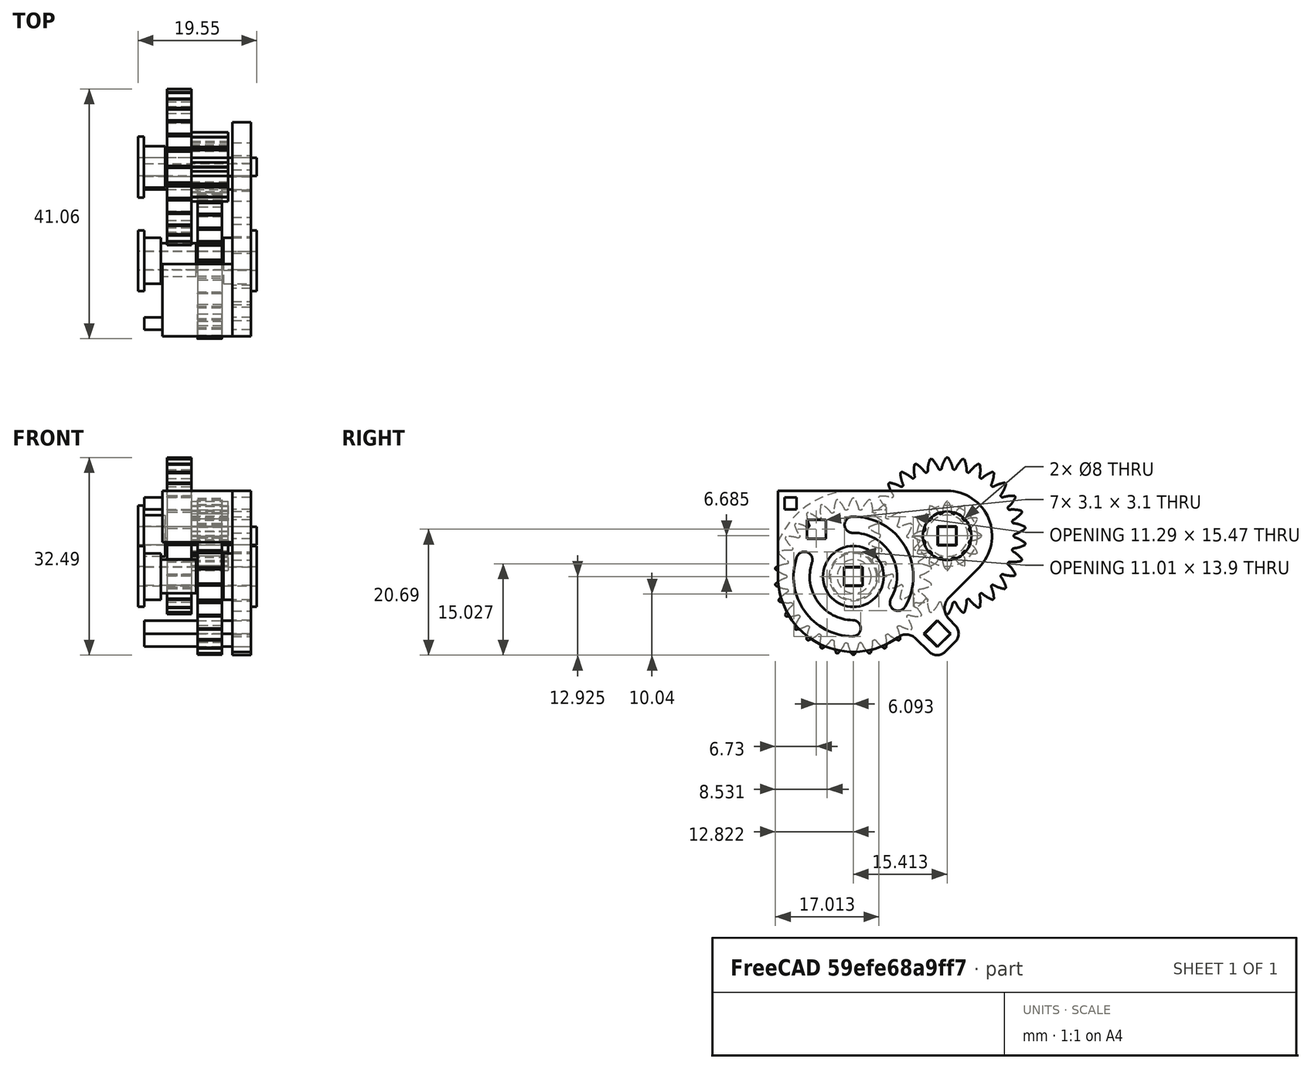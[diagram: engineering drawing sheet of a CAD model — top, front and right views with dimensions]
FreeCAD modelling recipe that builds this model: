
FCSTD DOCUMENT  (FreeCAD 1.1R14555 (Git shallow))
Label: testbuild
License: All rights reserved
LicenseURL: https://en.wikipedia.org/wiki/All_rights_reserved
objects: Sketcher::SketchObject×17, App::Point×14, PartDesign::Body×13, PartDesign::Pad×13, PartDesign::SubShapeBinder×6, App::Link×3, PartDesign::FeaturePython×3, PartDesign::Pocket×3, PartDesign::Point×3, App::FeaturePython×2, Assembly::JointGroup×1, Assembly::AssemblyObject×1, Part::DatumPoint×1, PartDesign::FeatureBase×1, App::DocumentObjectGroup×1
note: 112 computed .brp shape members not serialized (recipe doc carries the construction recipe); baked Part::Feature solids carry a one-line shape summary decoded from their .brp
EXTERNAL_REF file=../toy_motor_with_body.FCStd obj=Body
EXTERNAL_REF file=../dot8_worm_gear .FCStd obj=Body007
EXTERNAL_REF file=../toy_motor_with_body.FCStd obj=Body001

FEATURE [App::Link] toymotor
  LinkedObject = -> <external ../toy_motor_with_body.FCStd>#Body
FEATURE [App::FeaturePython] GroundedJoint  # Assembly grounded joint (typed FeaturePython)
  ObjectToGround = -> toymotor
FEATURE [App::Link] dot8_worm_gear
  LinkPlacement = pos=(-5.5e-15,18.25,2.4e-15) rot=(-0.41468,0.643445,0.643444;2.3554rad)
  LinkedObject = -> <external ../dot8_worm_gear .FCStd>#Body007
  Placement = pos=(-5.5e-15,18.25,2.4e-15) rot=(-0.41468,0.643445,0.643444;2.3554rad)
FEATURE [PartDesign::FeaturePython] InvoluteGear  # WARN: FeaturePython — macro-defined, semantics opaque (R4)
  AttacherType = Attacher::AttachEngine3D
  Suppressed = false
  addendum_diameter = 25.76
  angular_backlash = 0
  axle_hole = true
  axle_holesize = 2.09
  backlash = 0
  clearance = 0.3
  double_helix = false
  head = 0.1
  head_fillet = 0
  height = 4
  helix_angle = 0
  module = 0.8
  num_teeth = 30
  numpoints = 20
  offset_hole = false
  offset_holeoffset = 10
  offset_holesize = 10
  pitch_diameter = 24
  pressure_angle = 26
  properties_from_tool = false
  reversed_backlash = false
  root_diameter = 21.92
  root_fillet = 0.3
  shift = 0
  simple = false
  transverse_pitch = 2.51327
  traverse_module = 0.8
  undercut = false
  version = 1.3.0
  expr: angular_backlash = backlash / pitch_diameter * 360 ° / pi
FEATURE [PartDesign::FeaturePython] InvoluteGear001  # WARN: FeaturePython — macro-defined, semantics opaque (R4)
  AttacherType = Attacher::AttachEngine3D
  Suppressed = false
  addendum_diameter = 11.36
  angular_backlash = 0
  axle_hole = true
  axle_holesize = 2.09
  backlash = 0
  clearance = 0.3
  double_helix = false
  head = 0.1
  head_fillet = 0
  height = 6
  helix_angle = 0
  module = 0.8
  num_teeth = 12
  numpoints = 20
  offset_hole = false
  offset_holeoffset = 10
  offset_holesize = 10
  pitch_diameter = 9.6
  pressure_angle = 27
  properties_from_tool = false
  reversed_backlash = false
  root_diameter = 7.52
  root_fillet = 0.4
  shift = 0
  simple = false
  transverse_pitch = 2.51327
  traverse_module = 0.8
  undercut = false
  version = 1.3.0
  expr: angular_backlash = backlash / pitch_diameter * 360 ° / pi
FEATURE [PartDesign::FeaturePython] InvoluteGear002  # WARN: FeaturePython — macro-defined, semantics opaque (R4)
  AttacherType = Attacher::AttachEngine3D
  Suppressed = false
  addendum_diameter = 25.76
  angular_backlash = 0
  axle_hole = true
  axle_holesize = 2.09
  backlash = 0
  clearance = 0.3
  double_helix = false
  head = 0.1
  head_fillet = 0
  height = 4
  helix_angle = 0
  module = 0.8
  num_teeth = 30
  numpoints = 20
  offset_hole = false
  offset_holeoffset = 10
  offset_holesize = 10
  pitch_diameter = 24
  pressure_angle = 26
  properties_from_tool = false
  reversed_backlash = false
  root_diameter = 21.92
  root_fillet = 0.3
  shift = 0
  simple = false
  transverse_pitch = 2.51327
  traverse_module = 0.8
  undercut = false
  version = 1.3.0
  expr: angular_backlash = backlash / pitch_diameter * 360 ° / pi
FEATURE [App::FeaturePython] Joint009  label="Revolute002"  # Assembly joint (typed FeaturePython)
  Angle = 0
  AngleMax = 0
  AngleMin = 0
  Detach1 = false
  Detach2 = false
  Distance = 0
  Distance2 = 0
  EnableAngleMax = false
  EnableAngleMin = false
  EnableLengthMax = false
  EnableLengthMin = false
  JointType = 1 (Revolute)
  LengthMax = 0
  LengthMin = 0
  Offset2 = pos=(0,0,-7) rot=(0,0,1;0rad)
  Placement1 = pos=(0,21.25,0) rot=(-1,0,0;1.5708rad)
  Placement2 = pos=(-8.07778e-06,1.0786e-06,2.99997) rot=(-0.13236,-0.991265,0;3e-06rad)
  Reference1 = -> Assembly [toymotor.Edge79,toymotor.Edge79]
  Reference2 = -> Assembly [dot8_worm_gear.Edge14,dot8_worm_gear.Edge14]
  Suppressed = false
FEATURE [Assembly::JointGroup] Joints
  Group = -> [GroundedJoint,Joint009]
FEATURE [App::Link] toymotor_body  label="toymotor.body"
  LinkPlacement = pos=(4e-15,4.2e-15,-3.5e-15) rot=(0,0,1;0rad)
  LinkedObject = -> <external ../toy_motor_with_body.FCStd>#Body001
  Placement = pos=(4e-15,4.2e-15,-3.5e-15) rot=(0,0,1;0rad)
FEATURE [Assembly::AssemblyObject] Assembly
  Group = -> [Joints,toymotor,GroundedJoint,toymotor_body,dot8_worm_gear,Joint009]
  Origin = -> Origin001
  Type = Assembly
FEATURE [Sketcher::SketchObject] Sketch006
  ArcFitTolerance = 1e-06
  AttachmentSupport = -> [InvoluteGear001]
  ExternalTypes = [0]
  FullyConstrained = true
  MakeInternals = false
  MapMode = 5
  Placement = pos=(0,0,6) rot=(0,0,1;0rad)
  sketch-geometry (5):
    g0: LineSegment StartX=-1.55 StartY=-1.55 StartZ=0 EndX=1.55 EndY=-1.55 EndZ=0
    g1: LineSegment StartX=1.55 StartY=-1.55 StartZ=0 EndX=1.55 EndY=1.55 EndZ=0
    g2: LineSegment StartX=1.55 StartY=1.55 StartZ=0 EndX=-1.55 EndY=1.55 EndZ=0
    g3: LineSegment StartX=-1.55 StartY=1.55 StartZ=0 EndX=-1.55 EndY=-1.55 EndZ=0
    g4: GeomPoint [constr] X=0 Y=0 Z=0
  constraints (12):
    c: Coincident(g0,g1)
    c: Coincident(g1,g2)
    c: Coincident(g2,g3)
    c: Coincident(g3,g0)
    c: Horizontal(g0)
    c: Horizontal(g2)
    c: Vertical(g1)
    c: Vertical(g3)
    c: Symmetric(g2,g0,g4)
    c: Coincident(g4,g-1)
    c: Equal(g2,g1)
    c: Distance(g2,g2) = 3.1
FEATURE [PartDesign::Pocket] Pocket001
  BaseFeature = -> InvoluteGear001
  Direction = (0,0,-1)
  Length = 5
  Length2 = 5
  Profile = -> Sketch006
  ReferenceAxis = -> Sketch006 [N_Axis]
  Refine = true
  SideType = 0
  Suppressed = false
  Type = 1
  Type2 = 0
FEATURE [Sketcher::SketchObject] Sketch007
  ArcFitTolerance = 1e-06
  AttachmentSupport = -> [InvoluteGear]
  ExternalTypes = [0]
  FullyConstrained = true
  MakeInternals = false
  MapMode = 5
  Placement = pos=(0,0,4) rot=(0,0,1;0rad)
  sketch-geometry (5):
    g0: LineSegment StartX=-1.55 StartY=1.55 StartZ=0 EndX=-1.55 EndY=-1.55 EndZ=0
    g1: LineSegment StartX=-1.55 StartY=-1.55 StartZ=0 EndX=1.55 EndY=-1.55 EndZ=0
    g2: LineSegment StartX=1.55 StartY=-1.55 StartZ=0 EndX=1.55 EndY=1.55 EndZ=0
    g3: LineSegment StartX=1.55 StartY=1.55 StartZ=0 EndX=-1.55 EndY=1.55 EndZ=0
    g4: GeomPoint [constr] X=0 Y=0 Z=0
  constraints (12):
    c: Coincident(g0,g1)
    c: Coincident(g1,g2)
    c: Coincident(g2,g3)
    c: Coincident(g3,g0)
    c: Vertical(g0)
    c: Vertical(g2)
    c: Horizontal(g1)
    c: Horizontal(g3)
    c: Symmetric(g2,g0,g4)
    c: Coincident(g4,g-1)
    c: Equal(g3,g2)
    c: Distance(g3,g3) = 3.1
FEATURE [PartDesign::Pocket] Pocket
  BaseFeature = -> InvoluteGear
  Direction = (0,0,-1)
  Length = 5
  Length2 = 5
  Profile = -> Sketch007
  ReferenceAxis = -> Sketch007 [N_Axis]
  Refine = true
  SideType = 0
  Suppressed = false
  Type = 1
  Type2 = 0
FEATURE [Sketcher::SketchObject] Sketch
  ArcFitTolerance = 1e-06
  AttachmentSupport = -> [InvoluteGear002]
  ExternalTypes = [0]
  FullyConstrained = true
  MakeInternals = false
  MapMode = 5
  Placement = pos=(0,0,4) rot=(0,0,1;0rad)
  sketch-geometry (5):
    g0: LineSegment StartX=1.55 StartY=1.55 StartZ=0 EndX=-1.55 EndY=1.55 EndZ=0
    g1: LineSegment StartX=-1.55 StartY=1.55 StartZ=0 EndX=-1.55 EndY=-1.55 EndZ=0
    g2: LineSegment StartX=-1.55 StartY=-1.55 StartZ=0 EndX=1.55 EndY=-1.55 EndZ=0
    g3: LineSegment StartX=1.55 StartY=-1.55 StartZ=0 EndX=1.55 EndY=1.55 EndZ=0
    g4: GeomPoint [constr] X=0 Y=0 Z=0
  constraints (12):
    c: Coincident(g0,g1)
    c: Coincident(g1,g2)
    c: Coincident(g2,g3)
    c: Coincident(g3,g0)
    c: Horizontal(g0)
    c: Horizontal(g2)
    c: Vertical(g1)
    c: Vertical(g3)
    c: Symmetric(g2,g0,g4)
    c: Coincident(g4,g-1)
    c: Equal(g3,g0)
    c: Distance(g0,g0) = 3.1
FEATURE [PartDesign::Pocket] Pocket002
  BaseFeature = -> InvoluteGear002
  Direction = (0,0,-1)
  Length = 5
  Length2 = 5
  Profile = -> Sketch
  ReferenceAxis = -> Sketch [N_Axis]
  Refine = true
  SideType = 0
  Suppressed = false
  Type = 1
  Type2 = 0
FEATURE [Sketcher::SketchObject] Sketch008
  ArcFitTolerance = 1e-06
  ExternalTypes = [0]
  FullyConstrained = false
  MakeInternals = false
  Placement = pos=(0,0,0) rot=(0.57735,0.57735,0.57735;2.0944rad)
  sketch-geometry (5):
    g0: LineSegment StartX=0 StartY=0 StartZ=0 EndX=25.3053 EndY=0 EndZ=0
    g1: LineSegment StartX=25.3053 StartY=-16.23 StartZ=0 EndX=9.89253 EndY=-22.9148 EndZ=0
    g2: LineSegment StartX=9.89253 StartY=-22.9148 StartZ=0 EndX=0 EndY=0 EndZ=0
    g3: LineSegment StartX=25.3053 StartY=0 StartZ=0 EndX=25.3053 EndY=-4.23 EndZ=0
    g4: LineSegment StartX=25.3053 StartY=-4.23 StartZ=0 EndX=25.3053 EndY=-16.23 EndZ=0
  constraints (12):
    c: Coincident(g0,g-1)
    c: PointOnObject(g0,g-1)
    c: Coincident(g1,g4)
    c: Coincident(g2,g1)
    c: Coincident(g2,g0)
    c: Distance(g1,g1) = 16.8
    c: Coincident(g3,g4)
    c: Parallel(g4,g3)
    c: Coincident(g3,g0)
    c: Vertical(g3)
    c: DistanceY(g4,g4) = 12
    c: DistanceY(g3,g3) = 4.23
FEATURE [PartDesign::Body] Body004  label="master"
  AllowCompound = false
  Group = -> [Sketch008]
  Origin = -> Origin005
FEATURE [PartDesign::Point] DatumPoint003
  AttacherType = Attacher::AttachEnginePoint
  AttachmentSupport = -> [Pocket]
  MapMode = 37
  Placement = pos=(0,-1e-16,2) rot=(0,0,1;0rad)
FEATURE [PartDesign::Body] Body  label="30_inv_gear"
  AllowCompound = false
  Group = -> [InvoluteGear,Sketch007,Pocket,DatumPoint003]
  Origin = -> Origin
  Placement = pos=(2,25.3053,-16.23) rot=(0,1,0;4.71239rad)
  Tip = -> Pocket
FEATURE [PartDesign::Point] DatumPoint
  AttacherType = Attacher::AttachEnginePoint
  AttachmentSupport = -> [Pocket001]
  MapMode = 37
  Placement = pos=(2e-16,0,3) rot=(0,0,1;0rad)
FEATURE [PartDesign::Body] Body002  label="12_inv_gear"
  AllowCompound = false
  Group = -> [InvoluteGear001,Sketch006,Pocket001,DatumPoint]
  Origin = -> Origin003
  Placement = pos=(2,25.3053,-16.23) rot=(0,1,0;1.5708rad)
  Tip = -> Pocket001
FEATURE [PartDesign::Point] DatumPoint004
  AttacherType = Attacher::AttachEnginePoint
  AttachmentSupport = -> [Pocket002]
  MapMode = 37
  Placement = pos=(-2e-16,-2e-16,2) rot=(0,0,1;0rad)
FEATURE [PartDesign::Body] Body003  label="30_inv_gear001"
  AllowCompound = false
  Group = -> [InvoluteGear002,Sketch,Pocket002,DatumPoint004]
  Origin = -> Origin004
  Placement = pos=(3,9.89253,-22.9148) rot=(0,1,0;1.5708rad)
  Tip = -> Pocket002
FEATURE [App::Point] Origin006  label="Origin"
  Role = Origin
FEATURE [App::Point] Origin007  label="Origin"
  Role = Origin
FEATURE [App::Point] Origin008  label="Origin"
  Role = Origin
FEATURE [App::Point] Origin009  label="Origin"
  Role = Origin
FEATURE [App::Point] Origin010  label="Origin"
  Role = Origin
FEATURE [App::Point] Origin012
  Role = Origin
FEATURE [PartDesign::SubShapeBinder] Binder
  BindCopyOnChange = 0
  BindMode = 0
  ClaimChildren = false
  Context = -> Body005 [Binder.]
  Fuse = false
  MakeFace = true
  OffsetFill = false
  OffsetIntersection = false
  OffsetJoinType = 0
  OffsetOpenResult = false
  PartialLoad = false
  Refine = true
  Relative = true
  Support = -> [Body004[Sketch008.Edge4]]
  _Version = 2
FEATURE [Sketcher::SketchObject] Sketch009
  ArcFitTolerance = 1e-06
  AttachmentSupport = -> [Origin011]
  ExternalGeometry = -> [Binder]
  ExternalTypes = [0]
  FullyConstrained = true
  MakeInternals = false
  MapMode = 5
  Placement = pos=(0,0,0) rot=(0.57735,0.57735,0.57735;2.0944rad)
  sketch-geometry (5):
    g0: LineSegment StartX=23.8053 StartY=-14.73 StartZ=0 EndX=23.8053 EndY=-17.73 EndZ=0
    g1: LineSegment StartX=23.8053 StartY=-17.73 StartZ=0 EndX=26.8053 EndY=-17.73 EndZ=0
    g2: LineSegment StartX=26.8053 StartY=-17.73 StartZ=0 EndX=26.8053 EndY=-14.73 EndZ=0
    g3: LineSegment StartX=26.8053 StartY=-14.73 StartZ=0 EndX=23.8053 EndY=-14.73 EndZ=0
    g4: GeomPoint [constr] X=25.3053 Y=-16.23 Z=0
  constraints (12):
    c: Coincident(g0,g1)
    c: Coincident(g1,g2)
    c: Coincident(g2,g3)
    c: Coincident(g3,g0)
    c: Vertical(g0)
    c: Vertical(g2)
    c: Horizontal(g1)
    c: Horizontal(g3)
    c: Symmetric(g2,g0,g4)
    c: Coincident(g4,g-3)
    c: Equal(g2,g3)
    c: Distance(g2,g2) = 3
FEATURE [PartDesign::Pad] Pad
  Direction = (1,0,0)
  Length = 12.75
  Length2 = 6.75
  Profile = -> Sketch009
  ReferenceAxis = -> Sketch009 [N_Axis]
  Refine = true
  SideType = 1
  Suppressed = false
  Type = 0
  Type2 = 0
FEATURE [PartDesign::Body] Body005  label="30r.shaft"
  AllowCompound = false
  Group = -> [Binder,Sketch009,Pad]
  Origin = -> Origin011
  Tip = -> Pad
FEATURE [App::Point] Origin014
  Role = Origin
FEATURE [Sketcher::SketchObject] Sketch010
  ArcFitTolerance = 1e-06
  AttachmentSupport = -> [Origin013]
  ExternalTypes = [0]
  FullyConstrained = false
  MakeInternals = false
  MapMode = 5
  Placement = pos=(0,0,0) rot=(0.57735,0.57735,0.57735;2.0944rad)
  sketch-geometry (3):
    g0: ArcOfCircle CenterX=12.5467 CenterY=-13.5228 CenterZ=0 NormalX=0 NormalY=0 NormalZ=1 AngleXU=0 Radius=13.54 StartAngle=1.62123 EndAngle=2.75617
    g1: LineSegment StartX=11.8641 StartY=0 StartZ=0 EndX=0 EndY=0 EndZ=0
    g2: LineSegment StartX=0 StartY=0 StartZ=0 EndX=0 EndY=-8.43248 EndZ=0
  constraints (6):
    c: Coincident(g1,g0)
    c: Horizontal(g1)
    c: Coincident(g2,g1)
    c: Coincident(g2,g0)
    c: Vertical(g2)
    c: Coincident(g1,g-1)
FEATURE [PartDesign::Pad] Pad001
  Direction = (1,0,0)
  Length = 9.5
  Length2 = 2
  Profile = -> Sketch010
  ReferenceAxis = -> Sketch010 [N_Axis]
  Refine = true
  Reversed = true
  SideType = 1
  Suppressed = false
  Type = 0
  Type2 = 0
FEATURE [Sketcher::SketchObject] Sketch011
  ArcFitTolerance = 1e-06
  AttachmentSupport = -> [Pad001]
  ExternalGeometry = -> [Pad001]
  ExternalTypes = [0]
  FullyConstrained = true
  MakeInternals = false
  MapMode = 5
  Placement = pos=(-9.5,0,0) rot=(0.57735,-0.57735,-0.57735;2.0944rad)
  sketch-geometry (5):
    g0: LineSegment StartX=-3.06066 StartY=-1.06066 StartZ=0 EndX=-3.06066 EndY=-3.06066 EndZ=0
    g1: LineSegment StartX=-3.06066 StartY=-3.06066 StartZ=0 EndX=-1.06066 EndY=-3.06066 EndZ=0
    g2: LineSegment StartX=-1.06066 StartY=-3.06066 StartZ=0 EndX=-1.06066 EndY=-1.06066 EndZ=0
    g3: LineSegment StartX=-1.06066 StartY=-1.06066 StartZ=0 EndX=-3.06066 EndY=-1.06066 EndZ=0
    g4: LineSegment [constr] StartX=0 StartY=0 StartZ=0 EndX=-3.47298 EndY=-3.47298 EndZ=0
  constraints (15):
    c: Coincident(g0,g1)
    c: Coincident(g1,g2)
    c: Coincident(g2,g3)
    c: Coincident(g3,g0)
    c: Vertical(g0)
    c: Vertical(g2)
    c: Horizontal(g1)
    c: Horizontal(g3)
    c: Equal(g1,g2)
    c: Distance(g1,g1) = 2
    c: Coincident(g4,g-1)
    c: PointOnObject(g4,g-3)
    c: PointOnObject(g2,g4)
    c: Angle(g-1,g4) = 0.785398
    c: Distance(g2,g4) = 1.5
FEATURE [PartDesign::Pad] Pad002
  BaseFeature = -> Pad001
  Direction = (-1,0,0)
  Length = 3
  Length2 = 14.5
  Profile = -> Sketch011
  ReferenceAxis = -> Sketch011 [N_Axis]
  Refine = true
  SideType = 1
  Suppressed = false
  Type = 0
  Type2 = 0
FEATURE [PartDesign::Body] Body006  label="mobo.bom.attch"
  AllowCompound = false
  Group = -> [Sketch010,Pad001,Sketch011,Pad002]
  Origin = -> Origin013
  Placement = pos=(6.75,-2.5,-8.85) rot=(0,0,1;0rad)
  Tip = -> Pad002
FEATURE [App::Point] Origin016
  Role = Origin
FEATURE [PartDesign::SubShapeBinder] Binder001
  BindCopyOnChange = 0
  BindMode = 0
  ClaimChildren = false
  Context = -> Body007 [Binder001.]
  Fuse = false
  MakeFace = true
  OffsetFill = false
  OffsetIntersection = false
  OffsetJoinType = 0
  OffsetOpenResult = false
  PartialLoad = false
  Refine = true
  Relative = true
  Support = -> [Body006[Pad002.Face4]]
  _Version = 2
FEATURE [PartDesign::SubShapeBinder] Binder002
  BindCopyOnChange = 0
  BindMode = 0
  ClaimChildren = false
  Context = -> Body007 [Binder002.]
  Fuse = false
  MakeFace = true
  OffsetFill = false
  OffsetIntersection = false
  OffsetJoinType = 0
  OffsetOpenResult = false
  PartialLoad = false
  Refine = true
  Relative = true
  Support = -> [Body004[Sketch008.Edge4]]
  _Version = 2
FEATURE [Sketcher::SketchObject] Sketch012
  ArcFitTolerance = 1e-06
  AttachmentSupport = -> [Origin015]
  ExternalGeometry = -> [Binder001,Binder002]
  ExternalTypes = [0,0,0,0,0,0,0]
  FullyConstrained = false
  MakeInternals = false
  MapMode = 5
  Placement = pos=(0,0,0) rot=(0.57735,0.57735,0.57735;2.0944rad)
  sketch-geometry (57):
    g0: LineSegment [constr] StartX=-26.2446 StartY=-5.81934 StartZ=0 EndX=-23.2446 EndY=-5.81934 EndZ=0
    g1: LineSegment [constr] StartX=-23.2446 StartY=-5.81934 StartZ=0 EndX=-23.2446 EndY=-2.81934 EndZ=0
    g2: LineSegment [constr] StartX=-23.2446 StartY=-2.81934 StartZ=0 EndX=-26.2446 EndY=-2.81934 EndZ=0
    g3: LineSegment [constr] StartX=-26.2446 StartY=-2.81934 StartZ=0 EndX=-26.2446 EndY=-5.81934 EndZ=0
    g4: GeomPoint [constr] X=-24.7446 Y=-4.31934 Z=0
    g5: LineSegment [constr] StartX=-10.8319 StartY=-12.5042 StartZ=0 EndX=-7.83187 EndY=-12.5042 EndZ=0
    g6: LineSegment [constr] StartX=-7.83187 StartY=-12.5042 StartZ=0 EndX=-7.83187 EndY=-9.50418 EndZ=0
    g7: LineSegment [constr] StartX=-7.83187 StartY=-9.50418 StartZ=0 EndX=-10.8319 EndY=-9.50418 EndZ=0
    g8: LineSegment [constr] StartX=-10.8319 StartY=-9.50418 StartZ=0 EndX=-10.8319 EndY=-12.5042 EndZ=0
    g9: GeomPoint [constr] X=-9.33187 Y=-11.0042 Z=0
    g10: Circle [constr] CenterX=-24.7446 CenterY=-4.31934 CenterZ=0 NormalX=0 NormalY=0 NormalZ=1 AngleXU=0 Radius=2.12132
    g11: Circle [constr] CenterX=-9.33187 CenterY=-11.0042 CenterZ=0 NormalX=0 NormalY=0 NormalZ=1 AngleXU=0 Radius=2.12132
    g12: Circle CenterX=-24.7446 CenterY=-4.31934 CenterZ=0 NormalX=0 NormalY=0 NormalZ=1 AngleXU=0 Radius=4
    g13: Circle CenterX=-9.33187 CenterY=-11.0042 CenterZ=0 NormalX=0 NormalY=0 NormalZ=1 AngleXU=0 Radius=4
    g14: LineSegment StartX=3.06066 StartY=3.06066 StartZ=0 EndX=3.06066 EndY=-11.0039 EndZ=0
    g15: ArcOfCircle CenterX=-24.7446 CenterY=-4.31934 CenterZ=0 NormalX=0 NormalY=0 NormalZ=1 AngleXU=0 Radius=7.38 StartAngle=1.5708 EndAngle=3.92699
    g16: LineSegment StartX=-24.7446 StartY=3.06066 StartZ=0 EndX=3.06066 EndY=3.06066 EndZ=0
    g17: LineSegment [constr] StartX=-42.8401 StartY=-3.41976 StartZ=0 EndX=-42.8401 EndY=-6.51976 EndZ=0
    g18: LineSegment [constr] StartX=-42.8401 StartY=-6.51976 StartZ=0 EndX=-39.7401 EndY=-6.51976 EndZ=0
    g19: LineSegment [constr] StartX=-39.7401 StartY=-6.51976 StartZ=0 EndX=-39.7401 EndY=-3.41976 EndZ=0
    g20: LineSegment [constr] StartX=-39.7401 StartY=-3.41976 StartZ=0 EndX=-42.8401 EndY=-3.41976 EndZ=0
    g21: GeomPoint [constr] X=-41.2901 Y=-4.96976 Z=0
    g22: ArcOfCircle CenterX=-9.33187 CenterY=-11.0042 CenterZ=0 NormalX=0 NormalY=0 NormalZ=1 AngleXU=0 Radius=12.3925 StartAngle=4.07512 EndAngle=6.28321
    g23: LineSegment StartX=-20.9101 StartY=-20.3929 StartZ=0 EndX=-23.1021 EndY=-18.2009 EndZ=0
    g24: LineSegment StartX=-23.1021 StartY=-18.2009 StartZ=0 EndX=-25.2941 EndY=-20.3929 EndZ=0
    g25: LineSegment StartX=-25.2941 StartY=-20.3929 StartZ=0 EndX=-23.1021 EndY=-22.5849 EndZ=0
    g26: LineSegment StartX=-23.1021 StartY=-22.5849 StartZ=0 EndX=-20.9101 EndY=-20.3929 EndZ=0
    g27: Circle [constr] CenterX=-23.1021 CenterY=-20.3929 CenterZ=0 NormalX=0 NormalY=0 NormalZ=1 AngleXU=0 Radius=2.19203
    g28: LineSegment StartX=-29.9631 StartY=-9.53779 StartZ=0 EndX=-25.0578 EndY=-14.4431 EndZ=0
    g29: LineSegment StartX=-25.0578 StartY=-18.0359 StartZ=0 EndX=-26.0847 EndY=-19.0627 EndZ=0
    g30: LineSegment StartX=-26.0847 StartY=-21.7237 StartZ=0 EndX=-24.4326 EndY=-23.3758 EndZ=0
    g31: LineSegment StartX=-21.7716 StartY=-23.3758 StartZ=0 EndX=-19.573 EndY=-21.1771 EndZ=0
    g32: ArcOfCircle CenterX=-26.8542 CenterY=-16.2395 CenterZ=0 NormalX=0 NormalY=0 NormalZ=1 AngleXU=0 Radius=2.54048 StartAngle=5.49779 EndAngle=7.06858
    g33: GeomPoint [constr] X=-23.2614 Y=-16.2395 Z=0
    g34: ArcOfCircle CenterX=-24.7542 CenterY=-20.3932 CenterZ=0 NormalX=0 NormalY=0 NormalZ=1 AngleXU=0 Radius=1.88157 StartAngle=2.35619 EndAngle=3.92699
    g35: GeomPoint [constr] X=-27.4151 Y=-20.3932 Z=0
    g36: ArcOfCircle CenterX=-23.1021 CenterY=-22.0453 CenterZ=0 NormalX=0 NormalY=0 NormalZ=1 AngleXU=0 Radius=1.88157 StartAngle=3.92699 EndAngle=5.49779
    g37: GeomPoint [constr] X=-23.1021 Y=-24.7063 Z=0
    g38: GeomPoint [constr] X=-17.4845 Y=-19.4449 Z=0
    g39: ArcOfCircle CenterX=-18.0158 CenterY=-22.7344 CenterZ=0 NormalX=0 NormalY=0 NormalZ=1 AngleXU=0 Radius=2.20224 StartAngle=0.933529 EndAngle=2.35619
    g40: LineSegment [constr] StartX=-25 StartY=-22.8084 StartZ=0 EndX=-23.9393 EndY=-21.7477 EndZ=0
    g41: LineSegment [constr] StartX=-21.8706 StartY=-21.3535 StartZ=0 EndX=-20.81 EndY=-22.4141 EndZ=0
    g42: ArcOfCircle CenterX=-9.33187 CenterY=-11.0042 CenterZ=0 NormalX=0 NormalY=0 NormalZ=1 AngleXU=0 Radius=9.83608 StartAngle=1.55622 EndAngle=3.67351
    g43: ArcOfCircle CenterX=-16.6618 CenterY=-15.3178 CenterZ=0 NormalX=0 NormalY=0 NormalZ=1 AngleXU=0 Radius=1.33107 StartAngle=3.67351 EndAngle=6.8151
    g44: ArcOfCircle CenterX=-9.20792 CenterY=-2.50008 CenterZ=0 NormalX=0 NormalY=0 NormalZ=1 AngleXU=0 Radius=1.33107 StartAngle=4.69781 EndAngle=7.83941
    g45: ArcOfCircle CenterX=-9.33187 CenterY=-11.0042 CenterZ=0 NormalX=0 NormalY=0 NormalZ=1 AngleXU=0 Radius=7.17393 StartAngle=1.55622 EndAngle=3.67351
    g46: ArcOfCircle CenterX=-9.33187 CenterY=-11.0042 CenterZ=0 NormalX=0 NormalY=0 NormalZ=1 AngleXU=0 Radius=9.83608 StartAngle=4.72652 EndAngle=6.61075
    g47: ArcOfCircle CenterX=-9.21166 CenterY=-19.5083 CenterZ=0 NormalX=0 NormalY=0 NormalZ=1 AngleXU=0 Radius=1.33107 StartAngle=1.58493 EndAngle=4.72652
    g48: ArcOfCircle CenterX=-1.2791 CenterY=-8.26776 CenterZ=0 NormalX=0 NormalY=0 NormalZ=1 AngleXU=0 Radius=1.33107 StartAngle=0.327569 EndAngle=3.46916
    g49: ArcOfCircle CenterX=-9.33187 CenterY=-11.0042 CenterZ=0 NormalX=0 NormalY=0 NormalZ=1 AngleXU=0 Radius=7.17393 StartAngle=4.72652 EndAngle=6.61075
    g50: LineSegment StartX=-4.78934 StartY=-1.68934 StartZ=0 EndX=-4.78934 EndY=-4.78934 EndZ=0
    g51: LineSegment StartX=-4.78934 StartY=-4.78934 StartZ=0 EndX=-1.68934 EndY=-4.78934 EndZ=0
    g52: LineSegment StartX=-1.68934 StartY=-4.78934 StartZ=0 EndX=-1.68934 EndY=-1.68934 EndZ=0
    g53: LineSegment StartX=-1.68934 StartY=-1.68934 StartZ=0 EndX=-4.78934 EndY=-1.68934 EndZ=0
    g54: GeomPoint [constr] X=-3.23934 Y=-3.23934 Z=0
    g55: LineSegment [constr] StartX=-28.6445 StartY=-18.2009 StartZ=0 EndX=-18.0503 EndY=-18.2009 EndZ=0
    g56: LineSegment [constr] StartX=-25.6512 StartY=-18.6293 StartZ=0 EndX=-24.5647 EndY=-19.6635 EndZ=0
  constraints (124):
    c: Coincident(g0,g1)
    c: Coincident(g1,g2)
    c: Coincident(g2,g3)
    c: Coincident(g3,g0)
    c: Horizontal(g0)
    c: Horizontal(g2)
    c: Vertical(g1)
    c: Vertical(g3)
    c: Symmetric(g2,g0,g4)
    c: Distance(g0,g2) = 3
    c: Coincident(g4,g-7)
    c: Coincident(g5,g6)
    c: Coincident(g6,g7)
    c: Coincident(g7,g8)
    c: Coincident(g8,g5)
    c: Horizontal(g5)
    c: Horizontal(g7)
    c: Vertical(g6)
    c: Vertical(g8)
    c: Symmetric(g7,g5,g9)
    c: Coincident(g9,g-7)
    c: Equal(g1,g2)
    c: Equal(g7,g6)
    c: Equal(g1,g7)
    c: Coincident(g10,g4)
    c: Coincident(g11,g9)
    c: Equal(g10,g11)
    c: PointOnObject(g1,g10)
    c: Coincident(g12,g4)
    c: Coincident(g13,g9)
    c: Coincident(g14,g-11)
    c: Vertical(g14)
    c: Coincident(g15,g4)
    c: Coincident(g16,g14)
    c: Horizontal(g16)
    c: Tangent(g16,g15) = 1.5708
    c: Coincident(g22,g14) = 1.5708
    c: Coincident(g17,g18)
    c: Coincident(g18,g19)
    c: Coincident(g19,g20)
    c: Coincident(g20,g17)
    c: Vertical(g17)
    c: Vertical(g19)
    c: Horizontal(g18)
    c: Horizontal(g20)
    c: Symmetric(g19,g17,g21)
    c: Distance(g17,g19) = 3.1
    c: Equal(g19,g20)
    c: Coincident(g9,g22)
    c: Coincident(g23,g24)
    c: Coincident(g24,g25)
    c: Coincident(g25,g26)
    c: Coincident(g26,g23)
    c: Equal(g23,g24)
    c: Equal(g23,g25)
    c: Equal(g23,g26)
    c: PointOnObject(g23,g27)
    c: PointOnObject(g24,g27)
    c: PointOnObject(g25,g27)
    c: PointOnObject(g26,g27)
    c: Distance(g26,g26) = 3.1
    c: Tangent(g28,g15) = -1.5708
    c: Parallel(g23,g28)
    c: PointOnObject(g33,g28)
    c: PointOnObject(g33,g29)
    c: Tangent(g28,g32) = 1.5708
    c: Tangent(g29,g32) = 1.5708
    c: PointOnObject(g35,g29)
    c: PointOnObject(g35,g30)
    c: Tangent(g29,g34) = -1.5708
    c: Tangent(g30,g34) = -1.5708
    c: PointOnObject(g37,g30)
    c: PointOnObject(g37,g31)
    c: Tangent(g30,g36) = -1.5708
    c: Tangent(g31,g36) = -1.5708
    c: Tangent(g31,g39) = 1.5708
    c: Tangent(g22,g39) = 1.5708
    c: Equal(g34,g36)
    c: Parallel(g30,g25)
    c: Parallel(g31,g26)
    c: PointOnObject(g40,g30)
    c: PointOnObject(g40,g25)
    c: PointOnObject(g41,g26)
    c: PointOnObject(g41,g31)
    c: Perpendicular(g25,g40)
    c: Perpendicular(g26,g41)
    c: Equal(g41,g40)
    c: Distance(g40,g40) = 1.5
    c: Coincident(g42,g45)
    c: Tangent(g45,g44) = 1.5708
    c: Tangent(g45,g43) = 1.5708
    c: Tangent(g42,g44) = -1.5708
    c: Tangent(g42,g43) = -1.5708
    c: Coincident(g42,g9)
    c: Coincident(g46,g49)
    c: Tangent(g49,g48) = 1.5708
    c: Tangent(g49,g47) = 1.5708
    c: Tangent(g46,g48) = -1.5708
    c: Tangent(g46,g47) = -1.5708
    c: Coincident(g46,g9)
    c: Equal(g12,g13)
    c: Diameter(g13) = 8
    c: Equal(g44,g48)
    c: Equal(g49,g45)
    c: Coincident(g50,g51)
    c: Coincident(g51,g52)
    c: Coincident(g52,g53)
    c: Coincident(g53,g50)
    c: Vertical(g50)
    c: Vertical(g52)
    c: Horizontal(g51)
    c: Horizontal(g53)
    c: Symmetric(g52,g50,g54)
    c: Equal(g52,g53)
    c: Distance(g53,g53) = 3.1
    c: Distance(g16,g53) = 4.75
    c: Distance(g14,g52) = 4.75
    c: Horizontal(g55)
    c: PointOnObject(g23,g55)
    c: Angle(g23,g55) = 0.785398
    c: Parallel(g24,g29)
    c: PointOnObject(g56,g29)
    c: PointOnObject(g56,g24)
    c: Equal(g56,g40)
FEATURE [PartDesign::Pad] Pad003
  Direction = (1,0,0)
  Length = 3
  Length2 = 10
  Profile = -> Sketch012
  ReferenceAxis = -> Sketch012 [N_Axis]
  Refine = true
  SideType = 0
  Suppressed = false
  Type = 0
  Type2 = 0
FEATURE [App::Point] Origin018
  Role = Origin
FEATURE [App::Point] Origin020
  Role = Origin
FEATURE [App::Point] Origin022
  Role = Origin
FEATURE [Sketcher::SketchObject] Sketch013
  ArcFitTolerance = 1e-06
  AttachmentSupport = -> [Origin021]
  ExternalTypes = [0]
  FullyConstrained = true
  MakeInternals = false
  MapMode = 5
  sketch-geometry (5):
    g0: LineSegment StartX=-1.5 StartY=1.5 StartZ=0 EndX=-1.5 EndY=-1.5 EndZ=0
    g1: LineSegment StartX=-1.5 StartY=-1.5 StartZ=0 EndX=1.5 EndY=-1.5 EndZ=0
    g2: LineSegment StartX=1.5 StartY=-1.5 StartZ=0 EndX=1.5 EndY=1.5 EndZ=0
    g3: LineSegment StartX=1.5 StartY=1.5 StartZ=0 EndX=-1.5 EndY=1.5 EndZ=0
    g4: GeomPoint [constr] X=0 Y=0 Z=0
  constraints (12):
    c: Coincident(g0,g1)
    c: Coincident(g1,g2)
    c: Coincident(g2,g3)
    c: Coincident(g3,g0)
    c: Vertical(g0)
    c: Vertical(g2)
    c: Horizontal(g1)
    c: Horizontal(g3)
    c: Symmetric(g2,g0,g4)
    c: Coincident(g4,g-1)
    c: Equal(g2,g3)
    c: Distance(g3,g3) = 3
FEATURE [PartDesign::Pad] Pad004
  Direction = (0,0,1)
  Length = 8.75
  Length2 = 8.75
  Profile = -> Sketch013
  ReferenceAxis = -> Sketch013 [N_Axis]
  Refine = true
  SideType = 1
  Suppressed = false
  Type = 0
  Type2 = 0
FEATURE [PartDesign::Body] Body010  label="rear.30r.shaft"
  AllowCompound = false
  Group = -> [Sketch013,Pad004]
  Origin = -> Origin021
  Placement = pos=(3,9.89253,-22.9148) rot=(0,1,0;1.5708rad)
  Tip = -> Pad004
FEATURE [Part::DatumPoint] DatumPoint005
  AttacherType = Attacher::AttachEnginePoint
  AttachmentSupport = -> [Pad003]
  MapMode = 37
  Placement = pos=(3,-23.1021,-20.3929) rot=(0,0,1;0rad)
FEATURE [PartDesign::Body] Body007  label="gear.housing.left"
  AllowCompound = false
  Group = -> [Binder001,Binder002,Sketch012,Pad003,DatumPoint005]
  Origin = -> Origin015
  Placement = pos=(-2.75,0.56066,-11.9107) rot=(0,0,1;3.14159rad)
  Tip = -> Pad003
FEATURE [PartDesign::FeatureBase] Clone
  BaseFeature = -> Body007
  Placement = pos=(-2.75,0.56066,-11.9107) rot=(0,0,1;3.14159rad)
  Suppressed = false
FEATURE [PartDesign::Body] Body008  label="gear.housing.right"
  AllowCompound = false
  Group = -> [Clone]
  Origin = -> Origin017
  Placement = pos=(14.5,4e-16,0) rot=(0,0,1;0rad)
  Tip = -> Clone
FEATURE [Sketcher::SketchObject] Sketch014
  ArcFitTolerance = 1e-06
  AttachmentSupport = -> [Origin019]
  ExternalTypes = [0]
  FullyConstrained = true
  MakeInternals = false
  MapMode = 5
  Placement = pos=(0,0,0) rot=(0.57735,0.57735,0.57735;2.0944rad)
  sketch-geometry (5):
    g0: LineSegment StartX=0 StartY=2.12132 StartZ=0 EndX=-2.12132 EndY=0 EndZ=0
    g1: LineSegment StartX=-2.12132 StartY=0 StartZ=0 EndX=0 EndY=-2.12132 EndZ=0
    g2: LineSegment StartX=0 StartY=-2.12132 StartZ=0 EndX=2.12132 EndY=0 EndZ=0
    g3: LineSegment StartX=2.12132 StartY=0 StartZ=0 EndX=0 EndY=2.12132 EndZ=0
    g4: Circle [constr] CenterX=0 CenterY=0 CenterZ=0 NormalX=0 NormalY=0 NormalZ=1 AngleXU=0 Radius=2.12132
  constraints (14):
    c: Coincident(g0,g1)
    c: Coincident(g1,g2)
    c: Coincident(g2,g3)
    c: Coincident(g3,g0)
    c: Equal(g0,g1)
    c: Equal(g0,g2)
    c: Equal(g0,g3)
    c: PointOnObject(g0,g4)
    c: PointOnObject(g1,g4)
    c: PointOnObject(g2,g4)
    c: PointOnObject(g3,g4)
    c: Coincident(g4,g-1)
    c: PointOnObject(g3,g-2)
    c: Distance(g3,g3) = 3
FEATURE [PartDesign::Pad] Pad005
  Direction = (1,0,0)
  Length = 17.5
  Length2 = 10
  Profile = -> Sketch014
  ReferenceAxis = -> Sketch014 [N_Axis]
  Refine = true
  Reversed = true
  SideType = 0
  Suppressed = false
  Type = 0
  Type2 = 0
FEATURE [PartDesign::Body] Body009  label="gear.housing.suport"
  AllowCompound = false
  Group = -> [Sketch014,Pad005]
  Origin = -> Origin019
  Placement = pos=(-5.75,23.7436,-32.3239) rot=(0,0,1;3.14159rad)
  Tip = -> Pad005
FEATURE [App::Point] Origin024
  Role = Origin
FEATURE [PartDesign::SubShapeBinder] Binder003
  BindCopyOnChange = 0
  BindMode = 0
  ClaimChildren = false
  Context = -> Body011 [Binder003.]
  Fuse = false
  MakeFace = true
  OffsetFill = false
  OffsetIntersection = false
  OffsetJoinType = 0
  OffsetOpenResult = false
  PartialLoad = false
  Refine = true
  Relative = true
  Support = -> [Body007[Pad003.Edge77]]
  _Version = 2
FEATURE [Sketcher::SketchObject] Sketch015
  ArcFitTolerance = 1e-06
  AttachmentSupport = -> [Origin023]
  ExternalGeometry = -> [Binder003]
  ExternalTypes = [0]
  FullyConstrained = true
  MakeInternals = false
  MapMode = 5
  sketch-geometry (6):
    g0: Circle CenterX=0 CenterY=-3.6e-15 CenterZ=0 NormalX=0 NormalY=0 NormalZ=1 AngleXU=0 Radius=5
    g1: LineSegment StartX=-1.55 StartY=-1.55 StartZ=0 EndX=1.55 EndY=-1.55 EndZ=0
    g2: LineSegment StartX=1.55 StartY=-1.55 StartZ=0 EndX=1.55 EndY=1.55 EndZ=0
    g3: LineSegment StartX=1.55 StartY=1.55 StartZ=0 EndX=-1.55 EndY=1.55 EndZ=0
    g4: LineSegment StartX=-1.55 StartY=1.55 StartZ=0 EndX=-1.55 EndY=-1.55 EndZ=0
    g5: GeomPoint [constr] X=0 Y=-3.6e-15 Z=0
  constraints (14):
    c: Coincident(g0,g-3)
    c: Coincident(g1,g2)
    c: Coincident(g2,g3)
    c: Coincident(g3,g4)
    c: Coincident(g4,g1)
    c: Horizontal(g1)
    c: Horizontal(g3)
    c: Vertical(g2)
    c: Vertical(g4)
    c: Symmetric(g3,g1,g5)
    c: Coincident(g5,g0)
    c: Equal(g2,g3)
    c: Distance(g3,g3) = 3.1
    c: Distance(g-3,g0) = 1
FEATURE [PartDesign::Pad] Pad006
  Direction = (0,0,1)
  Length = 1
  Length2 = 8.2
  Profile = -> Sketch015
  ReferenceAxis = -> Sketch015 [N_Axis]
  Refine = true
  SideType = 0
  Suppressed = false
  Type = 0
  Type2 = 0
FEATURE [Sketcher::SketchObject] Sketch016
  ArcFitTolerance = 1e-06
  AttachmentSupport = -> [Origin023]
  ExternalGeometry = -> [Binder003]
  ExternalTypes = [0]
  FullyConstrained = true
  MakeInternals = false
  MapMode = 5
  sketch-geometry (6):
    g0: LineSegment StartX=-1.55 StartY=1.55 StartZ=0 EndX=-1.55 EndY=-1.55 EndZ=0
    g1: LineSegment StartX=-1.55 StartY=-1.55 StartZ=0 EndX=1.55 EndY=-1.55 EndZ=0
    g2: LineSegment StartX=1.55 StartY=-1.55 StartZ=0 EndX=1.55 EndY=1.55 EndZ=0
    g3: LineSegment StartX=1.55 StartY=1.55 StartZ=0 EndX=-1.55 EndY=1.55 EndZ=0
    g4: GeomPoint [constr] X=0 Y=-3.6e-15 Z=0
    g5: Circle CenterX=0 CenterY=-3.6e-15 CenterZ=0 NormalX=0 NormalY=0 NormalZ=1 AngleXU=0 Radius=3.8
  constraints (14):
    c: Coincident(g0,g1)
    c: Coincident(g1,g2)
    c: Coincident(g2,g3)
    c: Coincident(g3,g0)
    c: Vertical(g0)
    c: Vertical(g2)
    c: Horizontal(g1)
    c: Horizontal(g3)
    c: Symmetric(g2,g0,g4)
    c: Coincident(g4,g-3)
    c: Equal(g2,g3)
    c: DistanceY(g2,g2) = 3.1
    c: Coincident(g5,g-3)
    c: Distance(g5,g-3) = 0.2
FEATURE [PartDesign::Pad] Pad007
  BaseFeature = -> Pad006
  Direction = (0,0,1)
  Length = 2.75
  Length2 = 10
  Profile = -> Sketch016
  ReferenceAxis = -> Sketch016 [N_Axis]
  Refine = true
  Reversed = true
  SideType = 0
  Suppressed = false
  Type = 0
  Type2 = 0
  UseCustomVector = true
FEATURE [Sketcher::SketchObject] Sketch017
  ArcFitTolerance = 1e-06
  AttachmentSupport = -> [Pad007]
  ExternalGeometry = -> [Pad007]
  ExternalTypes = [0,0,0,0]
  FullyConstrained = false
  MakeInternals = false
  MapMode = 5
  Placement = pos=(0,0,-2.75) rot=(1,0,0;3.14159rad)
  sketch-geometry (2):
    g0: Circle CenterX=0 CenterY=-0.125026 CenterZ=0 NormalX=0 NormalY=0 NormalZ=1 AngleXU=0 Radius=2.78215
    g1: LineSegment [constr] StartX=0 StartY=-0.125026 StartZ=0 EndX=1.88959 EndY=1.91698 EndZ=0
  constraints (5):
    c: PointOnObject(g0,g-2)
    c: Coincident(g1,g0)
    c: PointOnObject(g1,g0)
    c: PointOnObject(g-6,g1)
    c: Distance(g-6,g1) = 0.5
FEATURE [PartDesign::Pad] Pad008
  BaseFeature = -> Pad007
  Direction = (0,0,-1)
  Length = 5.75
  Length2 = 10
  Profile = -> Sketch017
  ReferenceAxis = -> Sketch017 [N_Axis]
  Refine = true
  SideType = 0
  Suppressed = false
  Type = 0
  Type2 = 0
FEATURE [PartDesign::Body] Body011  label="shaft.stopper"
  AllowCompound = false
  Group = -> [Binder003,Sketch015,Pad006,Sketch016,Pad007,Sketch017,Pad008]
  Origin = -> Origin023
  Placement = pos=(-5.75,9.89253,-22.9148) rot=(0,1,0;4.71239rad)
  Tip = -> Pad008
FEATURE [App::Point] Origin026
  Role = Origin
FEATURE [PartDesign::SubShapeBinder] Binder004
  BindCopyOnChange = 0
  BindMode = 0
  ClaimChildren = false
  Context = -> Body012 [Binder004.]
  Fuse = false
  MakeFace = true
  OffsetFill = false
  OffsetIntersection = false
  OffsetJoinType = 0
  OffsetOpenResult = false
  PartialLoad = false
  Refine = true
  Relative = true
  Support = -> [Body008[Clone.Edge45]]
  _Version = 2
FEATURE [Sketcher::SketchObject] Sketch018
  ArcFitTolerance = 1e-06
  AttachmentSupport = -> [Origin025]
  ExternalGeometry = -> [Binder004]
  ExternalTypes = [0]
  FullyConstrained = true
  MakeInternals = false
  MapMode = 5
  sketch-geometry (6):
    g0: Circle CenterX=3.6e-15 CenterY=-7.1e-15 CenterZ=0 NormalX=0 NormalY=0 NormalZ=1 AngleXU=0 Radius=5
    g1: LineSegment StartX=-1.55 StartY=-1.55 StartZ=0 EndX=1.55 EndY=-1.55 EndZ=0
    g2: LineSegment StartX=1.55 StartY=-1.55 StartZ=0 EndX=1.55 EndY=1.55 EndZ=0
    g3: LineSegment StartX=1.55 StartY=1.55 StartZ=0 EndX=-1.55 EndY=1.55 EndZ=0
    g4: LineSegment StartX=-1.55 StartY=1.55 StartZ=0 EndX=-1.55 EndY=-1.55 EndZ=0
    g5: GeomPoint [constr] X=3.6e-15 Y=-7.1e-15 Z=0
  constraints (14):
    c: Coincident(g0,g-3)
    c: Coincident(g1,g2)
    c: Coincident(g2,g3)
    c: Coincident(g3,g4)
    c: Coincident(g4,g1)
    c: Horizontal(g1)
    c: Horizontal(g3)
    c: Vertical(g2)
    c: Vertical(g4)
    c: Symmetric(g3,g1,g5)
    c: Coincident(g5,g0)
    c: Equal(g2,g3)
    c: Distance(g3,g3) = 3.1
    c: Distance(g-3,g0) = 1
FEATURE [PartDesign::Pad] Pad009
  Direction = (0,0,1)
  Length = 1
  Length2 = 10
  Profile = -> Sketch018
  ReferenceAxis = -> Sketch018 [N_Axis]
  Refine = true
  SideType = 0
  Suppressed = false
  Type = 0
  Type2 = 0
FEATURE [Sketcher::SketchObject] Sketch019
  ArcFitTolerance = 1e-06
  AttachmentSupport = -> [Pad009]
  ExternalGeometry = -> [Binder004]
  ExternalTypes = [0]
  FullyConstrained = true
  MakeInternals = false
  MapMode = 5
  Placement = pos=(0,0,0) rot=(1,0,0;3.14159rad)
  sketch-geometry (6):
    g0: Circle CenterX=3.6e-15 CenterY=7.1e-15 CenterZ=0 NormalX=0 NormalY=0 NormalZ=1 AngleXU=0 Radius=3.8
    g1: LineSegment StartX=-1.55 StartY=-1.55 StartZ=0 EndX=1.55 EndY=-1.55 EndZ=0
    g2: LineSegment StartX=1.55 StartY=-1.55 StartZ=0 EndX=1.55 EndY=1.55 EndZ=0
    g3: LineSegment StartX=1.55 StartY=1.55 StartZ=0 EndX=-1.55 EndY=1.55 EndZ=0
    g4: LineSegment StartX=-1.55 StartY=1.55 StartZ=0 EndX=-1.55 EndY=-1.55 EndZ=0
    g5: GeomPoint [constr] X=3.6e-15 Y=7.1e-15 Z=0
  constraints (14):
    c: Coincident(g0,g-3)
    c: Distance(g-3,g0) = 0.2
    c: Coincident(g1,g2)
    c: Coincident(g2,g3)
    c: Coincident(g3,g4)
    c: Coincident(g4,g1)
    c: Horizontal(g1)
    c: Horizontal(g3)
    c: Vertical(g2)
    c: Vertical(g4)
    c: Symmetric(g3,g1,g5)
    c: Coincident(g5,g0)
    c: Equal(g3,g4)
    c: DistanceY(g4,g4) = 3.1
FEATURE [PartDesign::Pad] Pad010
  BaseFeature = -> Pad009
  Direction = (0,0,-1)
  Length = 4.5
  Length2 = 10
  Profile = -> Sketch019
  ReferenceAxis = -> Sketch019 [N_Axis]
  Refine = true
  SideType = 0
  Suppressed = false
  Type = 0
  Type2 = 0
FEATURE [PartDesign::Body] Body012  label="shaft.stopper.2"
  AllowCompound = false
  Group = -> [Binder004,Sketch018,Pad009,Sketch019,Pad010]
  Origin = -> Origin025
  Placement = pos=(11.75,9.89253,-22.9148) rot=(0,1,0;1.5708rad)
  Tip = -> Pad010
FEATURE [App::Point] Origin028
  Role = Origin
FEATURE [PartDesign::SubShapeBinder] Binder005
  BindCopyOnChange = 0
  BindMode = 0
  ClaimChildren = false
  Context = -> Body013 [Binder005.]
  Fuse = false
  MakeFace = true
  OffsetFill = false
  OffsetIntersection = false
  OffsetJoinType = 0
  OffsetOpenResult = false
  PartialLoad = false
  Refine = true
  Relative = true
  Support = -> [Body007[Pad003.Edge75]]
  _Version = 2
FEATURE [Sketcher::SketchObject] Sketch020
  ArcFitTolerance = 1e-06
  AttachmentSupport = -> [Origin027]
  ExternalGeometry = -> [Binder005]
  ExternalTypes = [0]
  FullyConstrained = true
  MakeInternals = false
  MapMode = 5
  sketch-geometry (6):
    g0: Circle CenterX=-9.8e-15 CenterY=-1.42e-14 CenterZ=0 NormalX=0 NormalY=0 NormalZ=1 AngleXU=0 Radius=5
    g1: LineSegment StartX=-1.55 StartY=1.55 StartZ=0 EndX=-1.55 EndY=-1.55 EndZ=0
    g2: LineSegment StartX=-1.55 StartY=-1.55 StartZ=0 EndX=1.55 EndY=-1.55 EndZ=0
    g3: LineSegment StartX=1.55 StartY=-1.55 StartZ=0 EndX=1.55 EndY=1.55 EndZ=0
    g4: LineSegment StartX=1.55 StartY=1.55 StartZ=0 EndX=-1.55 EndY=1.55 EndZ=0
    g5: GeomPoint [constr] X=-9.8e-15 Y=-1.42e-14 Z=0
  constraints (14):
    c: Coincident(g0,g-3)
    c: Coincident(g1,g2)
    c: Coincident(g2,g3)
    c: Coincident(g3,g4)
    c: Coincident(g4,g1)
    c: Vertical(g1)
    c: Vertical(g3)
    c: Horizontal(g2)
    c: Horizontal(g4)
    c: Symmetric(g3,g1,g5)
    c: Equal(g3,g4)
    c: DistanceY(g3,g3) = 3.1
    c: Coincident(g5,g0)
    c: Distance(g0,g-3) = 1
FEATURE [PartDesign::Pad] Pad011
  Direction = (0,0,1)
  Length = 1
  Length2 = 10
  Profile = -> Sketch020
  ReferenceAxis = -> Sketch020 [N_Axis]
  Refine = true
  SideType = 0
  Suppressed = false
  Type = 0
  Type2 = 0
FEATURE [Sketcher::SketchObject] Sketch021
  ArcFitTolerance = 1e-06
  AttachmentSupport = -> [Pad011]
  ExternalGeometry = -> [Binder005]
  ExternalTypes = [0]
  FullyConstrained = false
  MakeInternals = false
  MapMode = 5
  Placement = pos=(0,0,0) rot=(1,0,0;3.14159rad)
  sketch-geometry (6):
    g0: LineSegment StartX=1.55 StartY=1.55 StartZ=0 EndX=-1.55 EndY=1.55 EndZ=0
    g1: LineSegment StartX=-1.55 StartY=1.55 StartZ=0 EndX=-1.55 EndY=-1.55 EndZ=0
    g2: LineSegment StartX=-1.55 StartY=-1.55 StartZ=0 EndX=1.55 EndY=-1.55 EndZ=0
    g3: LineSegment StartX=1.55 StartY=-1.55 StartZ=0 EndX=1.55 EndY=1.55 EndZ=0
    g4: GeomPoint [constr] X=-9.9e-15 Y=1.42e-14 Z=0
    g5: Circle CenterX=-9.9e-15 CenterY=1.42e-14 CenterZ=0 NormalX=0 NormalY=0 NormalZ=1 AngleXU=0 Radius=3.38774
  constraints (13):
    c: Coincident(g0,g1)
    c: Coincident(g1,g2)
    c: Coincident(g2,g3)
    c: Coincident(g3,g0)
    c: Horizontal(g0)
    c: Horizontal(g2)
    c: Vertical(g1)
    c: Vertical(g3)
    c: Symmetric(g2,g0,g4)
    c: Coincident(g4,g-3)
    c: Equal(g2,g3)
    c: DistanceY(g3,g3) = 3.1
    c: Coincident(g5,g4)
FEATURE [PartDesign::Pad] Pad012
  BaseFeature = -> Pad011
  Direction = (0,0,-1)
  Length = 3.5
  Length2 = 10
  Profile = -> Sketch021
  ReferenceAxis = -> Sketch021 [N_Axis]
  Refine = true
  SideType = 0
  Suppressed = false
  Type = 0
  Type2 = 0
FEATURE [PartDesign::Body] Body013  label="shaft.stopper.3"
  AllowCompound = false
  Group = -> [Binder005,Sketch020,Pad011,Sketch021,Pad012]
  Origin = -> Origin027
  Placement = pos=(-5.8,25.3053,-16.23) rot=(0,-1,0;1.5708rad)
  Tip = -> Pad012
FEATURE [App::DocumentObjectGroup] Group  label="CAD"
  Group = -> [Body,Body002,Body003,Body005,Body006,Body007,Body008,Body010,Body009,Body011,Body012,Body013]
